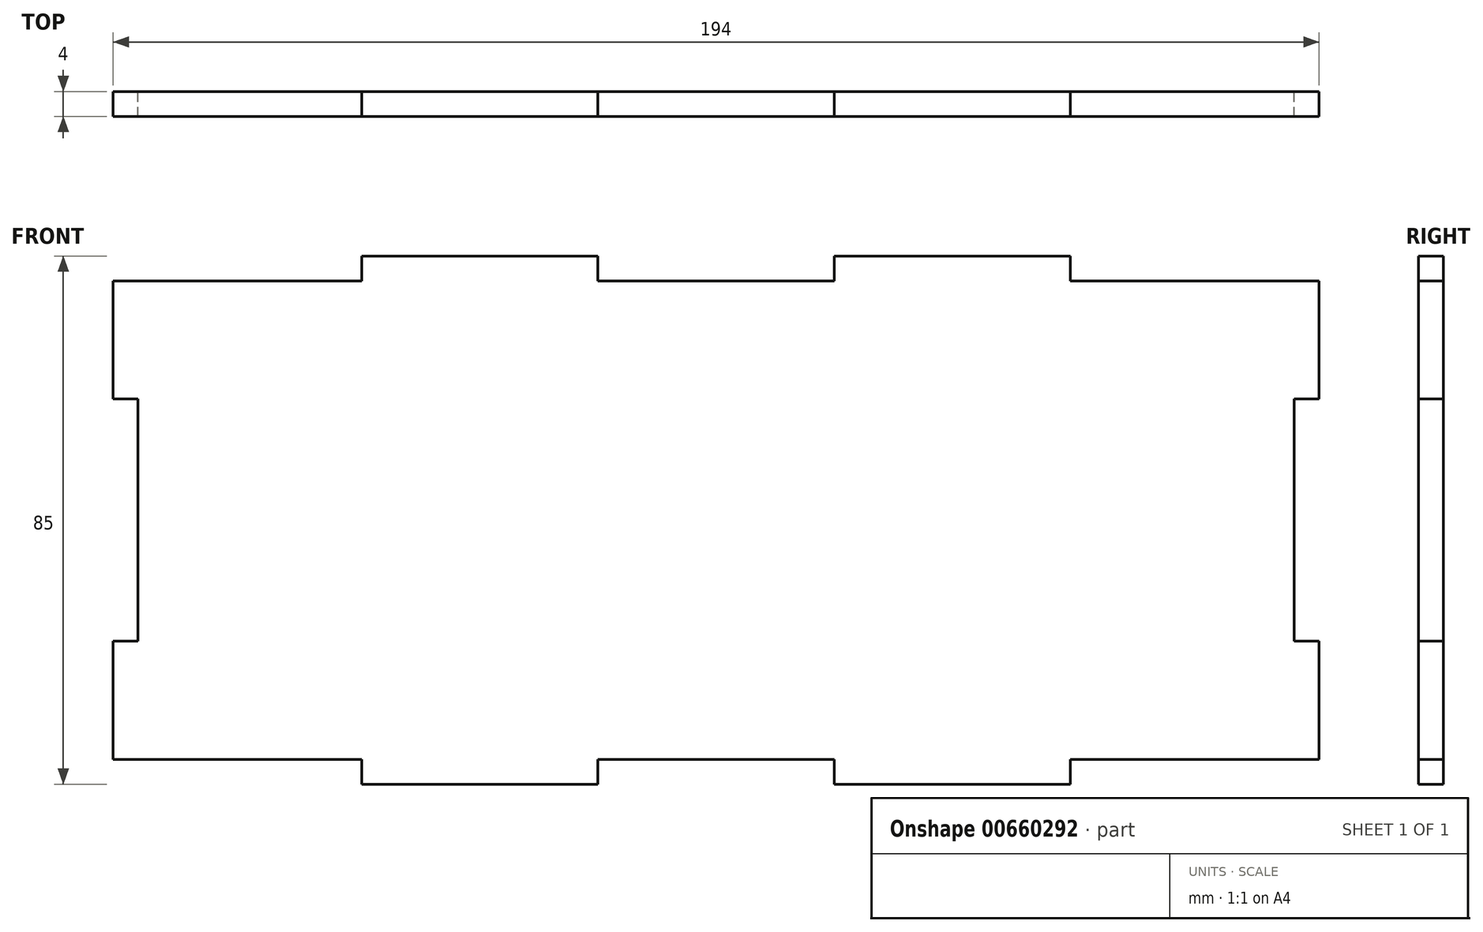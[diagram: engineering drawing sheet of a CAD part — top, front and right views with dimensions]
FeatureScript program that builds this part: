
annotation { "Feature Type Name" : "Feature", "Feature Type Description" : "" }
export const myFeature = defineFeature(function(context is Context, id is Id, definition is map)
    precondition{}
    {
        {
            var Q0;
            Q0=qCreatedBy(makeId("Front.planeOp"),FACE);
            var sketch = newSketch(context, id + "F0", { "sketchPlane" : qUnion([Q0])});
            skLineSegment(sketch, "E0.bottom", {"start": v(0, 0) * mm, "end": v(194, 0) * mm});
            skLineSegment(sketch, "E0.top", {"start": v(0, 85) * mm, "end": v(194, 85) * mm});
            skLineSegment(sketch, "E0.left", {"start": v(0, 0) * mm, "end": v(0, 85) * mm});
            skLineSegment(sketch, "E0.right", {"start": v(194, 0) * mm, "end": v(194, 85) * mm});
            skLineSegment(sketch, "E1.bottom", {"start": v(0, 0) * mm, "end": v(40, 0) * mm});
            skLineSegment(sketch, "E1.top", {"start": v(0, 4) * mm, "end": v(40, 4) * mm});
            skLineSegment(sketch, "E1.left", {"start": v(0, 0) * mm, "end": v(0, 4) * mm});
            skLineSegment(sketch, "E1.right", {"start": v(40, 0) * mm, "end": v(40, 4) * mm});
            skLineSegment(sketch, "E2.bottom", {"start": v(78, 0) * mm, "end": v(116, 0) * mm});
            skLineSegment(sketch, "E2.top", {"start": v(78, 4) * mm, "end": v(116, 4) * mm});
            skLineSegment(sketch, "E2.left", {"start": v(78, 0) * mm, "end": v(78, 4) * mm});
            skLineSegment(sketch, "E2.right", {"start": v(116, 0) * mm, "end": v(116, 4) * mm});
            skLineSegment(sketch, "E3.bottom", {"start": v(194, 0) * mm, "end": v(154, 0) * mm});
            skLineSegment(sketch, "E3.top", {"start": v(194, 4) * mm, "end": v(154, 4) * mm});
            skLineSegment(sketch, "E3.left", {"start": v(194, 0) * mm, "end": v(194, 4) * mm});
            skLineSegment(sketch, "E3.right", {"start": v(154, 0) * mm, "end": v(154, 4) * mm});
            skLineSegment(sketch, "E4.bottom", {"start": v(0, 62) * mm, "end": v(4, 62) * mm});
            skLineSegment(sketch, "E4.top", {"start": v(0, 23) * mm, "end": v(4, 23) * mm});
            skLineSegment(sketch, "E4.left", {"start": v(0, 62) * mm, "end": v(0, 23) * mm});
            skLineSegment(sketch, "E4.right", {"start": v(4, 62) * mm, "end": v(4, 23) * mm});
            skLineSegment(sketch, "E5.bottom", {"start": v(194, 62) * mm, "end": v(190, 62) * mm});
            skLineSegment(sketch, "E5.top", {"start": v(194, 23) * mm, "end": v(190, 23) * mm});
            skLineSegment(sketch, "E5.left", {"start": v(194, 62) * mm, "end": v(194, 23) * mm});
            skLineSegment(sketch, "E5.right", {"start": v(190, 62) * mm, "end": v(190, 23) * mm});
            skLineSegment(sketch, "E6.bottom", {"start": v(194, 85) * mm, "end": v(154, 85) * mm});
            skLineSegment(sketch, "E6.top", {"start": v(194, 81) * mm, "end": v(154, 81) * mm});
            skLineSegment(sketch, "E6.left", {"start": v(194, 85) * mm, "end": v(194, 81) * mm});
            skLineSegment(sketch, "E6.right", {"start": v(154, 85) * mm, "end": v(154, 81) * mm});
            skLineSegment(sketch, "E7.bottom", {"start": v(0, 85) * mm, "end": v(40, 85) * mm});
            skLineSegment(sketch, "E7.top", {"start": v(0, 81) * mm, "end": v(40, 81) * mm});
            skLineSegment(sketch, "E7.left", {"start": v(0, 85) * mm, "end": v(0, 81) * mm});
            skLineSegment(sketch, "E7.right", {"start": v(40, 85) * mm, "end": v(40, 81) * mm});
            skLineSegment(sketch, "E8.bottom", {"start": v(78, 85) * mm, "end": v(116, 85) * mm});
            skLineSegment(sketch, "E8.top", {"start": v(78, 81) * mm, "end": v(116, 81) * mm});
            skLineSegment(sketch, "E8.left", {"start": v(78, 85) * mm, "end": v(78, 81) * mm});
            skLineSegment(sketch, "E8.right", {"start": v(116, 85) * mm, "end": v(116, 81) * mm});
            skSolve(sketch);
        }
        {
            var Q0;
            {var subQ12=sQuery(id+"F0.wireOp",EDGE,"E1.top");Q0=makeQuery(id+"F0.imprint","IMPRINT",FACE,{"disambiguationData":[TD([[makeQuery(id+"F0.imprint","IMPRINT",EDGE,{"derivedFrom":subQ12}),1.0]])]});}
            extrude(context, id + "F1", {"entities" : qUnion([Q0]), "depth" : 4 * mm, "offsetDistance" : 25 * mm});
        }
    });
